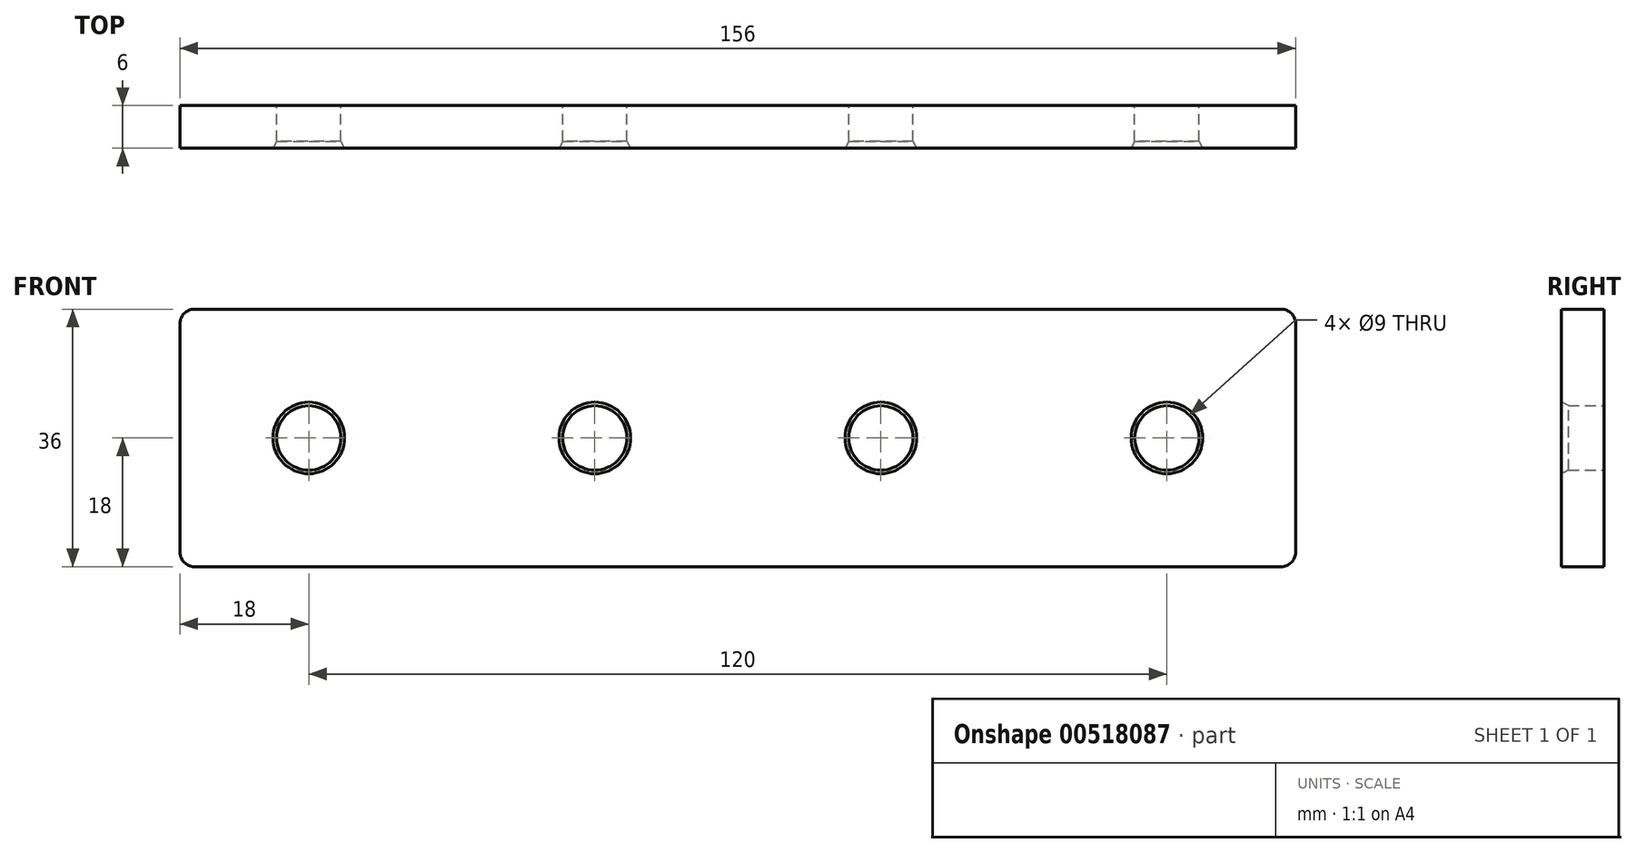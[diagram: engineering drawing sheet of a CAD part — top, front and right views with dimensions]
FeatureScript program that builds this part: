
annotation { "Feature Type Name" : "Feature", "Feature Type Description" : "" }
export const myFeature = defineFeature(function(context is Context, id is Id, definition is map)
    precondition{}
    {
        {
            var Q0;
            Q0=qCreatedBy(makeId("Front.planeOp"),FACE);
            var sketch = newSketch(context, id + "F0", { "sketchPlane" : qUnion([Q0])});
            skCircle(sketch, "E0", {"center": v(0, 0) * mm, "radius": 4.5 * mm});
            skCircle(sketch, "E1.1.0.0", {"center": v(40, 0) * mm, "radius": 4.5 * mm});
            skCircle(sketch, "E1.2.0.0", {"center": v(80, 0) * mm, "radius": 4.5 * mm});
            skCircle(sketch, "E1.3.0.0", {"center": v(120, 0) * mm, "radius": 4.5 * mm});
            skLineSegment(sketch, "E1.direction1", {"start": v(0, 0) * mm, "end": v(40, 0) * mm, "construction": true});
            skLineSegment(sketch, "E2.bottom", {"start": v(-16, 18) * mm, "end": v(136, 18) * mm});
            skLineSegment(sketch, "E2.top", {"start": v(-16, -18) * mm, "end": v(136, -18) * mm});
            skLineSegment(sketch, "E2.left", {"start": v(-18, 16) * mm, "end": v(-18, -16) * mm});
            skLineSegment(sketch, "E2.right", {"start": v(138, 16) * mm, "end": v(138, -16) * mm});
            skLineSegment(sketch, "E3", {"start": v(0, 0) * mm, "end": v(-18, 0) * mm, "construction": true});
            skLineSegment(sketch, "E4", {"start": v(120, 0) * mm, "end": v(138, 0) * mm, "construction": true});
            skPoint(sketch, "E5.visualSharp", {"position": v(-18, 18) * mm});
            skArc(sketch, "E5.filletArc", {"start": v(-16, 18) * mm, "mid": v(-17.41, 17.41) * mm, "end": v(-18, 16) * mm});
            skPoint(sketch, "E6.visualSharp", {"position": v(-18, -18) * mm});
            skArc(sketch, "E6.filletArc", {"start": v(-18, -16) * mm, "mid": v(-17.41, -17.41) * mm, "end": v(-16, -18) * mm});
            skPoint(sketch, "E7.visualSharp", {"position": v(138, -18) * mm});
            skArc(sketch, "E7.filletArc", {"start": v(136, -18) * mm, "mid": v(137.41, -17.41) * mm, "end": v(138, -16) * mm});
            skPoint(sketch, "E8.visualSharp", {"position": v(138, 18) * mm});
            skArc(sketch, "E8.filletArc", {"start": v(138, 16) * mm, "mid": v(137.41, 17.41) * mm, "end": v(136, 18) * mm});
            skSolve(sketch);
        }
        {
            var Q0;
            Q0=makeQuery(id+"F0.imprint","IMPRINT",FACE,{"disambiguationData":[TD([[makeQuery(id+"F0.imprint","IMPRINT",EDGE,{"derivedFrom":sQuery(id+"F0.wireOp",EDGE,"E0")}),-1.0]])]});
            extrude(context, id + "F1", {"entities" : qUnion([Q0]), "depth" : 6 * mm, "offsetDistance" : 25 * mm});
        }
        {
            var Q0;
            Q0=makeQuery(id+"F1.opExtrude","CAP_EDGE",EDGE,{"disambiguationData":[OSD([sQuery(id+"F0.wireOp",EDGE,"E0")])],"isStart":false});
            var Q1;
            Q1=makeQuery(id+"F1.opExtrude","CAP_EDGE",EDGE,{"disambiguationData":[OSD([sQuery(id+"F0.wireOp",EDGE,"E1.1.0.0")])],"isStart":false});
            var Q2;
            Q2=makeQuery(id+"F1.opExtrude","CAP_EDGE",EDGE,{"disambiguationData":[OSD([sQuery(id+"F0.wireOp",EDGE,"E1.2.0.0")])],"isStart":false});
            var Q3;
            Q3=makeQuery(id+"F1.opExtrude","CAP_EDGE",EDGE,{"disambiguationData":[OSD([sQuery(id+"F0.wireOp",EDGE,"E1.3.0.0")])],"isStart":false});
            chamfer(context, id + "F2", {"entities" : qUnion([Q0, Q1, Q2, Q3]), "chamferType" : ChamferType.TWO_OFFSETS, "width1" : 1 * mm, "oppositeDirection" : false, "width2" : .5 * mm, "tangentPropagation" : true});
        }
    });
